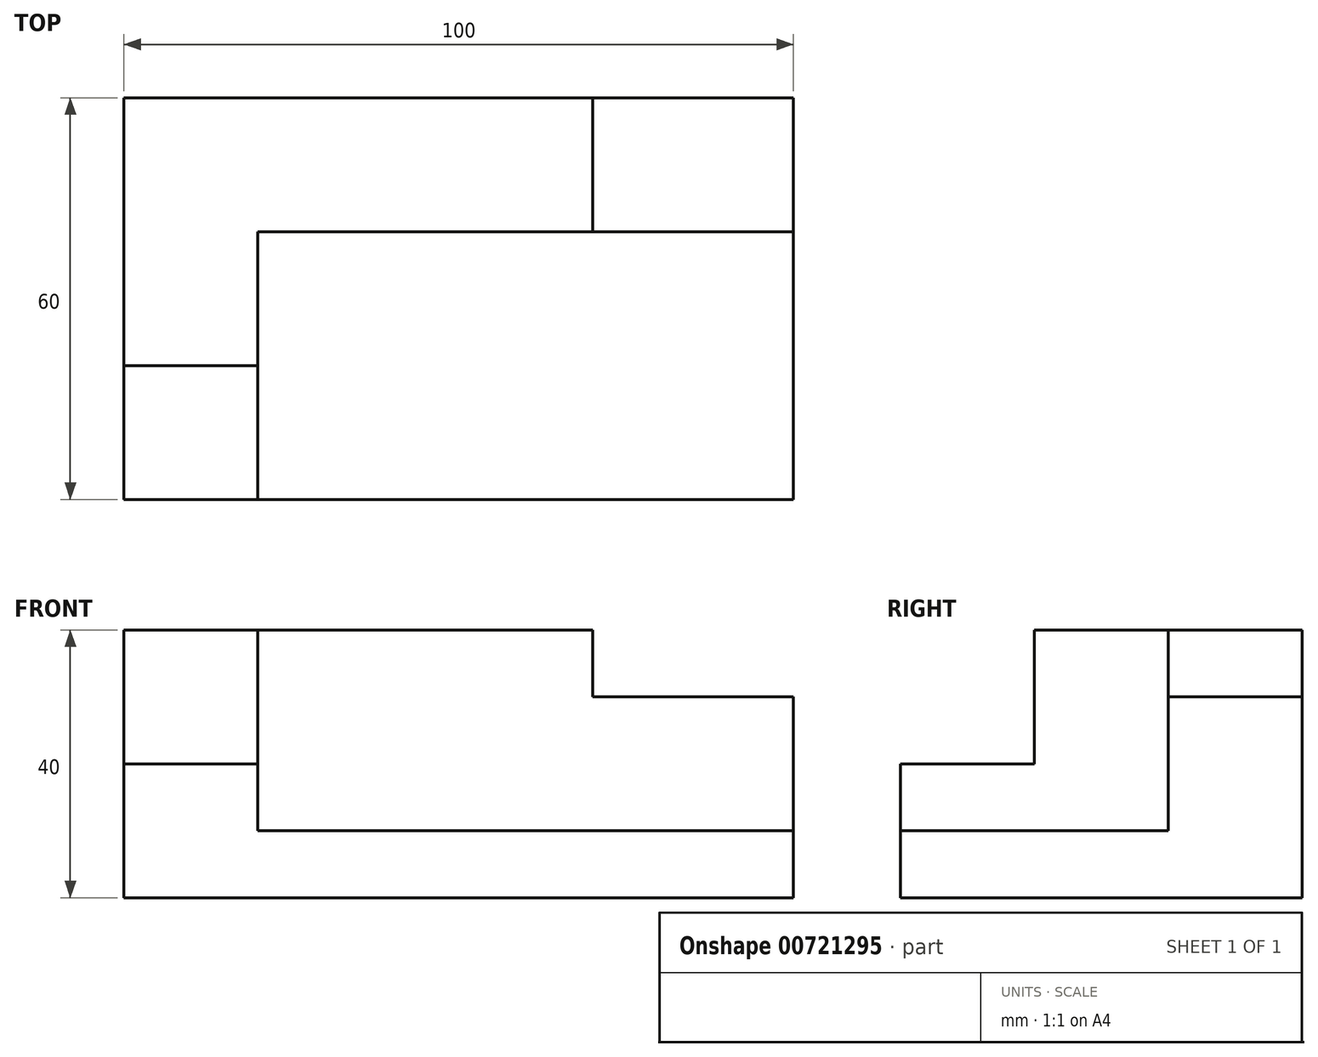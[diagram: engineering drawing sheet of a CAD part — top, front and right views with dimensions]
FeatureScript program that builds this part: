
annotation { "Feature Type Name" : "Feature", "Feature Type Description" : "" }
export const myFeature = defineFeature(function(context is Context, id is Id, definition is map)
    precondition{}
    {
        {
            var Q0;
            Q0=qCreatedBy(makeId("Front.planeOp"),FACE);
            var sketch = newSketch(context, id + "F0", { "sketchPlane" : qUnion([Q0])});
            skLineSegment(sketch, "E0", {"start": v(0, 0) * mm, "end": v(100, 0) * mm});
            skLineSegment(sketch, "E1", {"start": v(100, 0) * mm, "end": v(100, 40) * mm});
            skLineSegment(sketch, "E2", {"start": v(100, 40) * mm, "end": v(0, 40) * mm});
            skLineSegment(sketch, "E3", {"start": v(0, 40) * mm, "end": v(0, 0) * mm});
            skSolve(sketch);
        }
        {
            var Q0;
            Q0 = qSketchRegion(id + "F0", true);
            extrude(context, id + "F1", {"entities" : qUnion([Q0]), "oppositeDirection" : true, "depth" : 60 * mm, "offsetDistance" : 25 * mm});
        }
        {
            var Q0;
            Q0=makeQuery(id+"F1.opExtrude","SWEPT_FACE",FACE,{"disambiguationData":[OSD([sQuery(id+"F0.wireOp",EDGE,"E2")])]});
            var sketch = newSketch(context, id + "F2", { "sketchPlane" : qUnion([Q0])});
            skLineSegment(sketch, "E4.bottom", {"start": v(100, 0) * mm, "end": v(20, 0) * mm});
            skLineSegment(sketch, "E4.top", {"start": v(100, 40) * mm, "end": v(20, 40) * mm});
            skLineSegment(sketch, "E4.left", {"start": v(100, 0) * mm, "end": v(100, 40) * mm});
            skLineSegment(sketch, "E4.right", {"start": v(20, 0) * mm, "end": v(20, 40) * mm});
            skSolve(sketch);
        }
        {
            var Q0;
            Q0=makeQuery(id+"F2.imprint","IMPRINT",FACE,{"disambiguationData":[TD([[makeQuery(id+"F2.imprint","IMPRINT",EDGE,{"derivedFrom":sQuery(id+"F2.wireOp",EDGE,"E4.bottom")}),-1.0]])]});
            extrude(context, id + "F3", {"entities" : qUnion([Q0]), "operationType" : NewBodyOperationType.REMOVE, "oppositeDirection" : true, "depth" : 30 * mm, "offsetDistance" : 25 * mm});
        }
        {
            var Q0;
            Q0=makeQuery(id+"F3.boolean.opBoolean","COPY",FACE,{"derivedFrom":makeQuery(id+"F3.opExtrude","SWEPT_FACE",FACE,{"disambiguationData":[OSD([sQuery(id+"F2.wireOp",EDGE,"E4.top")])]})});
            var sketch = newSketch(context, id + "F4", { "sketchPlane" : qUnion([Q0])});
            skLineSegment(sketch, "E5.bottom", {"start": v(100, 40) * mm, "end": v(70, 40) * mm});
            skLineSegment(sketch, "E5.top", {"start": v(100, 30) * mm, "end": v(70, 30) * mm});
            skLineSegment(sketch, "E5.left", {"start": v(100, 40) * mm, "end": v(100, 30) * mm});
            skLineSegment(sketch, "E5.right", {"start": v(70, 40) * mm, "end": v(70, 30) * mm});
            skSolve(sketch);
        }
        {
            var Q0;
            Q0 = qSketchRegion(id + "F4", true);
            extrude(context, id + "F5", {"entities" : qUnion([Q0]), "operationType" : NewBodyOperationType.REMOVE, "oppositeDirection" : true, "depth" : 20 * mm, "offsetDistance" : 25 * mm});
        }
        {
            var Q0;
            Q0=makeQuery(id+"F1.opExtrude","CAP_FACE",FACE,{"disambiguationData":[OSD([sQuery(id+"F0.wireOp",EDGE,"E0"),sQuery(id+"F0.wireOp",EDGE,"E1"),sQuery(id+"F0.wireOp",EDGE,"E2"),sQuery(id+"F0.wireOp",EDGE,"E3")])],"isStart":true});
            var sketch = newSketch(context, id + "F6", { "sketchPlane" : qUnion([Q0])});
            skLineSegment(sketch, "E6.bottom", {"start": v(0, 40) * mm, "end": v(20, 40) * mm});
            skLineSegment(sketch, "E6.top", {"start": v(0, 20) * mm, "end": v(20, 20) * mm});
            skLineSegment(sketch, "E6.left", {"start": v(0, 40) * mm, "end": v(0, 20) * mm});
            skLineSegment(sketch, "E6.right", {"start": v(20, 40) * mm, "end": v(20, 20) * mm});
            skSolve(sketch);
        }
        {
            var Q0;
            Q0 = qSketchRegion(id + "F6", true);
            extrude(context, id + "F7", {"entities" : qUnion([Q0]), "operationType" : NewBodyOperationType.REMOVE, "oppositeDirection" : true, "depth" : 20 * mm, "offsetDistance" : 25 * mm});
        }
    });
